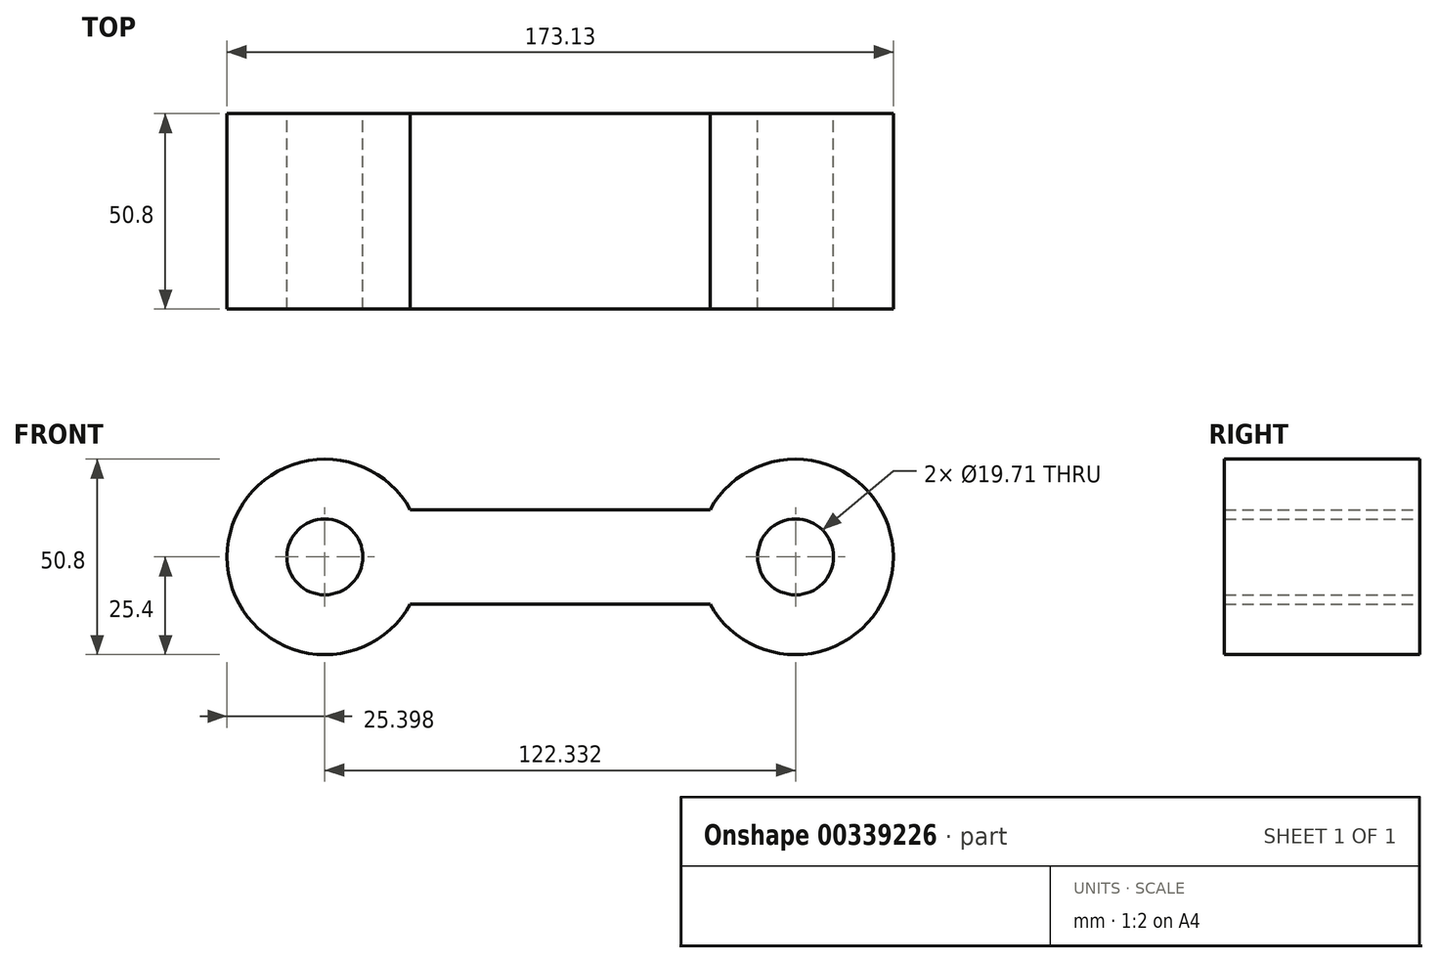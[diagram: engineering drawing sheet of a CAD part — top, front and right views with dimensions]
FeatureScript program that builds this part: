
annotation { "Feature Type Name" : "Feature", "Feature Type Description" : "" }
export const myFeature = defineFeature(function(context is Context, id is Id, definition is map)
    precondition{}
    {
        {
            var Q0;
            Q0=qCreatedBy(makeId("Front.planeOp"),FACE);
            var sketch = newSketch(context, id + "F0", { "sketchPlane" : qUnion([Q0])});
            skCircle(sketch, "E0", {"center": v(0, 0) * mm, "radius": 9.86 * mm});
            skCircle(sketch, "E1", {"center": v(0, 0) * mm, "radius": 25.4 * mm});
            skCircle(sketch, "E2", {"center": v(-122.33, 0) * mm, "radius": 9.86 * mm});
            skCircle(sketch, "E3", {"center": v(-122.33, 0) * mm, "radius": 25.4 * mm});
            skLineSegment(sketch, "E4", {"start": v(-100.1, 12.27) * mm, "end": v(-22.24, 12.27) * mm});
            skLineSegment(sketch, "E5", {"start": v(-122.33, 0) * mm, "end": v(0, 0) * mm, "construction": true});
            skLineSegment(sketch, "E6.MirrorCS", {"start": v(-100.1, -12.27) * mm, "end": v(-22.24, -12.27) * mm});
            skSolve(sketch);
        }
        {
            var Q0;
            Q0=makeQuery(id+"F0.imprint","IMPRINT",FACE,{"disambiguationData":[TD([[makeQuery(id+"F0.imprint","IMPRINT",EDGE,{"derivedFrom":sQuery(id+"F0.wireOp",EDGE,"E0")}),-1.0]])]});
            var Q1;
            Q1=makeQuery(id+"F0.imprint","IMPRINT",FACE,{"disambiguationData":[TD([[makeQuery(id+"F0.imprint","IMPRINT",EDGE,{"derivedFrom":sQuery(id+"F0.wireOp",EDGE,"E2")}),-1.0]])]});
            var Q2;
            {var subQ0=sQuery(id+"F0.wireOp",EDGE,"E4");Q2=makeQuery(id+"F0.imprint","IMPRINT",FACE,{"disambiguationData":[TD([[makeQuery(id+"F0.imprint","IMPRINT",EDGE,{"derivedFrom":subQ0}),-1.0]])]});}
            extrude(context, id + "F1", {"entities" : qUnion([Q0, Q1, Q2]), "depth" : 50.8 * mm});
        }
    });
